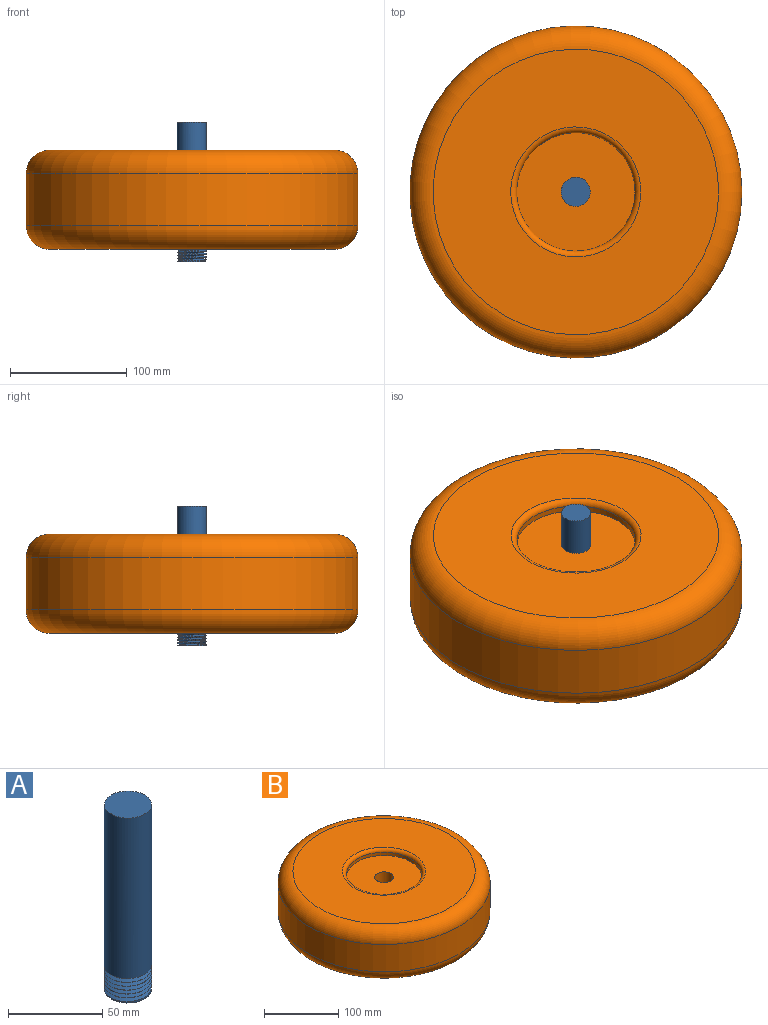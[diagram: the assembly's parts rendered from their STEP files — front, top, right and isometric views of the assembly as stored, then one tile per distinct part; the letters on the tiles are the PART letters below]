
ASSEMBLY  parts=2 mates=1
PART A: 13 faces, bbox 28.9x25x121.3 mm
  f0: cylinder r=12.5mm len=25mm, axis (0,0,-1), area 38.5mm2, adj f1,f8,f9,f10,f12
  f1: cylinder r=12.5mm len=25mm, axis (0,0,-1), area 7.9mm2, adj f0,f2,f10,f12
  f2: cylinder r=12.5mm len=25mm, axis (0,0,-1), area 7.8mm2, adj f1,f3,f10,f12
  f3: cylinder r=12.5mm len=25mm, axis (0,0,-1), area 7.9mm2, adj f2,f4,f10,f12
  f4: cylinder r=12.5mm len=25mm, axis (0,0,-1), area 7.9mm2, adj f3,f5,f10,f12
  f5: cylinder r=12.5mm len=25mm, axis (0,0,-1), area 7.9mm2, adj f4,f6,f10,f12
  f6: cylinder r=12.5mm len=105.1mm, axis (0,0,-1), area 8156.3mm2, adj f5,f7,f11,f12
  f7: plane 25x25mm, normal (0,0,1), area 490.9mm2, adj f6
  f8: plane 25x23.95mm, normal (0,0,-1), area 465mm2, adj f0,f9,f10
  f9: plane 1.69x1.4mm, normal (0.81,0.59,0), area 1.6mm2, adj f0,f8,f10,f12
  f10: bspline ~28.87x25mm, area 1076.6mm2, adj f0,f1,f2,f3,f4,f5,f8,f9
  f11: plane 2.4x2.08mm, normal (1,0,0), area 2.5mm2, adj f6,f10,f12
  f12: bspline ~28.87x25mm, area 1105.6mm2, adj f0,f1,f2,f3,f4,f5,f6,f9
PART B: 11 faces, bbox 308.5x308.5x85 mm
  f0: cylinder r=142.5mm len=285mm, axis (0,0,-1), area 40290.9mm2, adj f9,f10
  f1: plane 245x245mm, normal (0,0,1), area 37361.7mm2, adj f7,f10
  f2: plane 245x245mm, normal (0,0,-1), area 37361.7mm2, adj f8,f9
  f3: cylinder r=50.8mm len=101.6mm, axis (0,0,-1), area 1595.9mm2, adj f5,f7
  f4: plane 101.6x101.6mm, normal (0,0,-1), area 7616.4mm2, adj f6,f8
  f5: plane 101.6x101.6mm, normal (0,0,1), area 7616.4mm2, adj f3,f6
  f6: cylinder r=12.5mm len=70mm, axis (0,0,-1), area 5497.8mm2, adj f4,f5
  f7: torus R=55.8mm, axis (0,0,1), area 2596.5mm2, adj f1,f3
  f8: torus R=55.8mm, axis (0,0,1), area 2596.5mm2, adj f2,f4
  f9: torus R=122.5mm, axis (0,0,1), area 26693.8mm2, adj f0,f2
  f10: torus R=122.5mm, axis (0,0,1), area 26693.8mm2, adj f0,f1
PLACE A t=(-88.77,-54.72,-15.62)mm
PLACE B t=(-88.77,-54.72,-4.72)mm
MATE cylindrical A.f0 <-> B.f0  axis (0,0,1) through (-88.77,-54.72,104.38)mm
